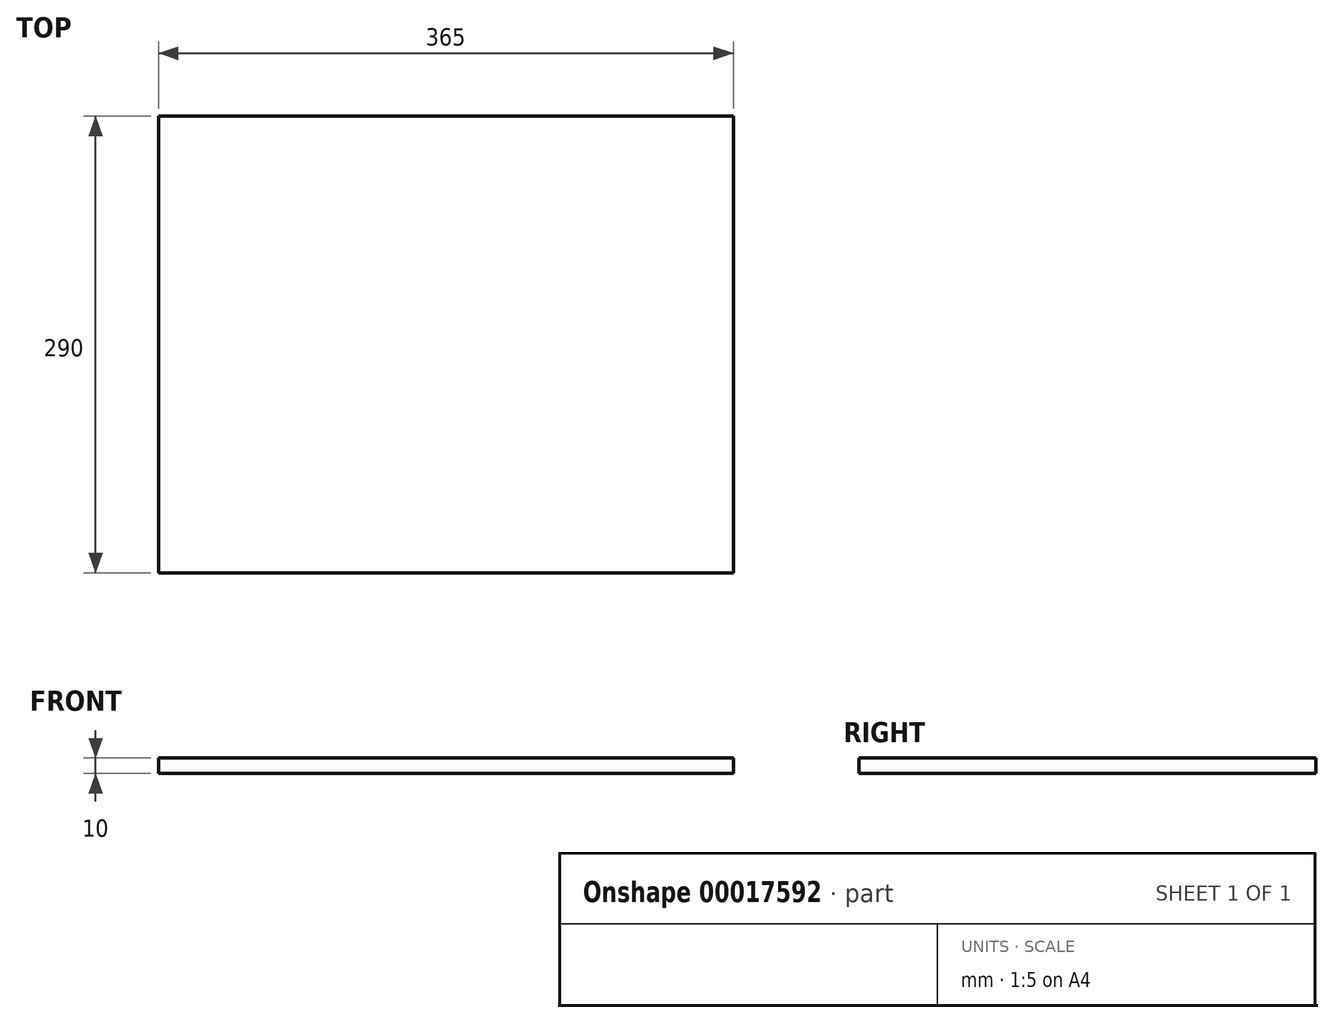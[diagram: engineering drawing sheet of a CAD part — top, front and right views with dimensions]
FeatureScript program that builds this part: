
annotation { "Feature Type Name" : "Feature", "Feature Type Description" : "" }
export const myFeature = defineFeature(function(context is Context, id is Id, definition is map)
    precondition{}
    {
        {
            var Q0;
            Q0=qCreatedBy(makeId("Top.planeOp"),FACE);
            var sketch = newSketch(context, id + "F0", { "sketchPlane" : qUnion([Q0])});
            skLineSegment(sketch, "E0.bottom", {"start": v(-70.96, 65.05) * mm, "end": v(294.04, 65.05) * mm});
            skLineSegment(sketch, "E0.top", {"start": v(-70.96, -224.95) * mm, "end": v(294.04, -224.95) * mm});
            skLineSegment(sketch, "E0.left", {"start": v(-70.96, 65.05) * mm, "end": v(-70.96, -224.95) * mm});
            skLineSegment(sketch, "E0.right", {"start": v(294.04, 65.05) * mm, "end": v(294.04, -224.95) * mm});
            skSolve(sketch);
        }
        {
            var Q0;
            Q0=qSketchRegion(id+"F0",true);
            extrude(context, id + "F1", {"entities" : qUnion([Q0]), "depth" : 10 * mm});
        }
    });
